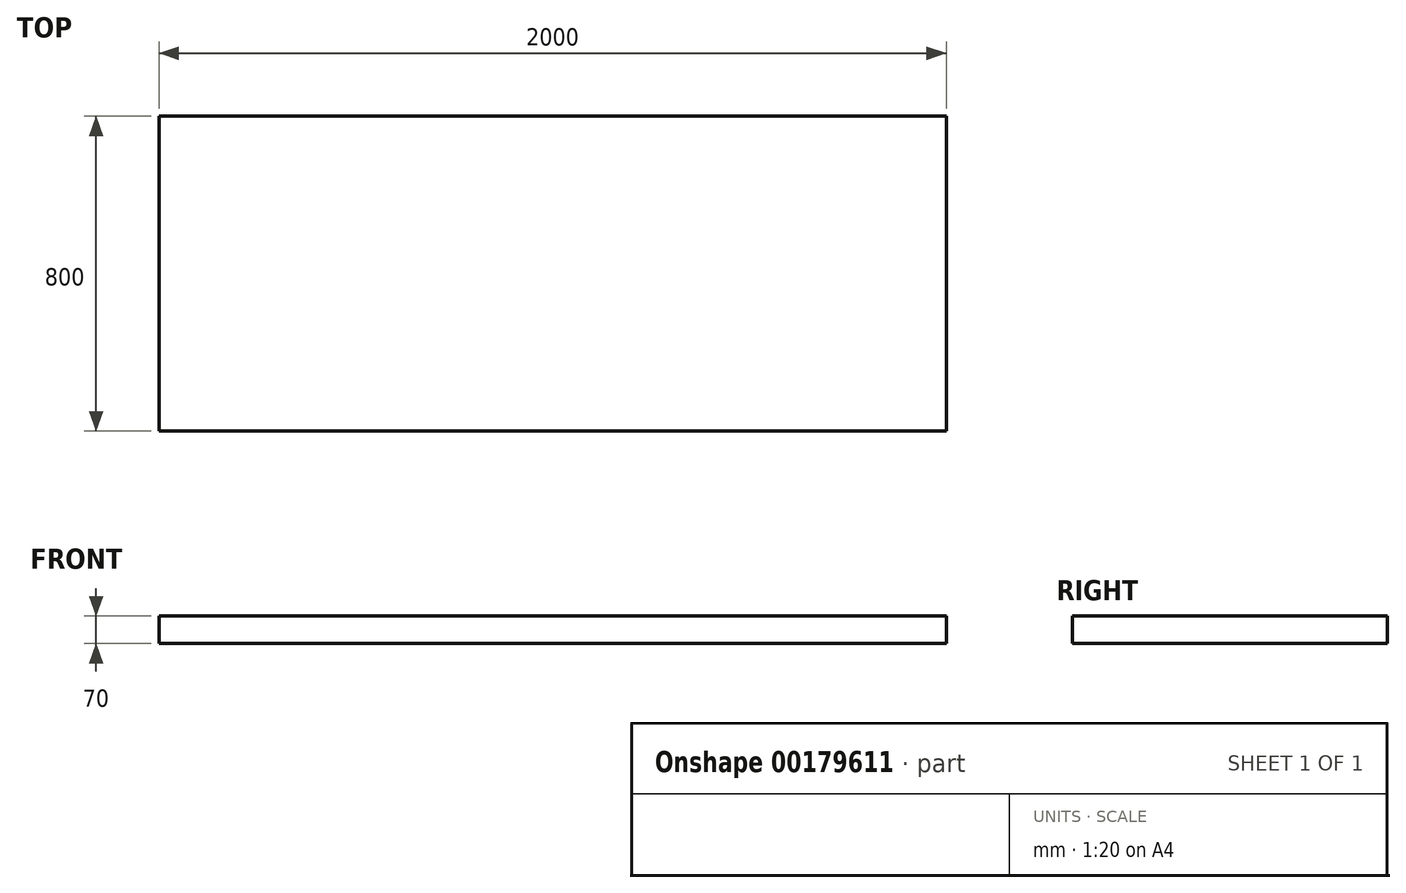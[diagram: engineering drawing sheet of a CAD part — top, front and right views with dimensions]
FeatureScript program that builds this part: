
annotation { "Feature Type Name" : "Feature", "Feature Type Description" : "" }
export const myFeature = defineFeature(function(context is Context, id is Id, definition is map)
    precondition{}
    {
        {
            var Q0;
            Q0=qCreatedBy(makeId("Top.planeOp"),FACE);
            var sketch = newSketch(context, id + "F0", { "sketchPlane" : qUnion([Q0])});
            skLineSegment(sketch, "E0.bottom", {"start": v(1000, -400) * mm, "end": v(-1000, -400) * mm});
            skLineSegment(sketch, "E0.top", {"start": v(1000, 400) * mm, "end": v(-1000, 400) * mm});
            skLineSegment(sketch, "E0.left", {"start": v(1000, -400) * mm, "end": v(1000, 400) * mm});
            skLineSegment(sketch, "E0.right", {"start": v(-1000, -400) * mm, "end": v(-1000, 400) * mm});
            skPoint(sketch, "E0.middle", {"position": v(0, 0) * mm});
            skSolve(sketch);
        }
        {
            var Q0;
            Q0=makeQuery(id+"F0.imprint","IMPRINT",FACE,{"disambiguationData":[TD([[makeQuery(id+"F0.imprint","IMPRINT",EDGE,{"derivedFrom":sQuery(id+"F0.wireOp",EDGE,"E0.bottom")}),-1.0]])]});
            extrude(context, id + "F1", {"entities" : qUnion([Q0]), "depth" : 70 * mm});
        }
    });
